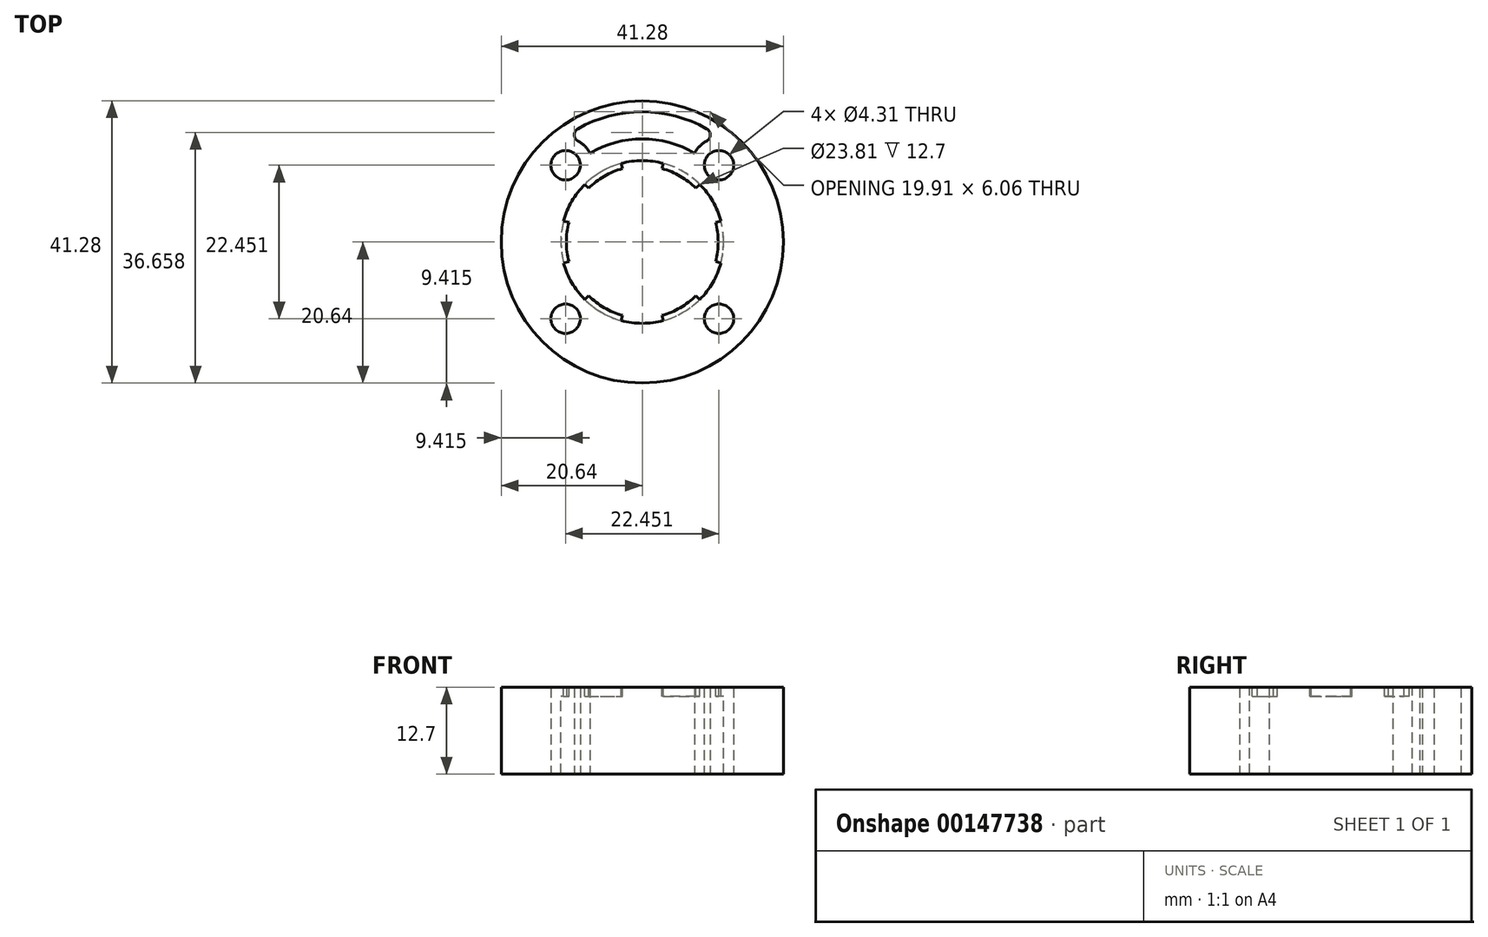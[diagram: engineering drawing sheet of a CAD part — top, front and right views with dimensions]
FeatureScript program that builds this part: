
annotation { "Feature Type Name" : "Feature", "Feature Type Description" : "" }
export const myFeature = defineFeature(function(context is Context, id is Id, definition is map)
    precondition{}
    {
        {
            var Q0;
            Q0=qCreatedBy(makeId("Top.planeOp"),FACE);
            var sketch = newSketch(context, id + "F0", { "sketchPlane" : qUnion([Q0])});
            skCircle(sketch, "E0", {"center": v(0, 0) * mm, "radius": 11.11 * mm});
            skLineSegment(sketch, "E1.bottom", {"start": v(11.23, 11.23) * mm, "end": v(-11.23, 11.23) * mm, "construction": true});
            skLineSegment(sketch, "E1.top", {"start": v(11.23, -11.23) * mm, "end": v(-11.23, -11.23) * mm, "construction": true});
            skLineSegment(sketch, "E1.left", {"start": v(11.23, 11.23) * mm, "end": v(11.23, -11.23) * mm, "construction": true});
            skLineSegment(sketch, "E1.right", {"start": v(-11.23, 11.23) * mm, "end": v(-11.23, -11.23) * mm, "construction": true});
            skCircle(sketch, "E2", {"center": v(-11.23, 11.23) * mm, "radius": 4.76 * mm, "construction": true});
            skLineSegment(sketch, "E3", {"start": v(0, 0) * mm, "end": v(0, 11.11) * mm});
            skCircle(sketch, "E4", {"center": v(-11.23, 11.23) * mm, "radius": 2.15 * mm});
            skCircle(sketch, "E5", {"center": v(-11.23, -11.23) * mm, "radius": 2.15 * mm});
            skCircle(sketch, "E6", {"center": v(11.23, -11.23) * mm, "radius": 2.15 * mm});
            skCircle(sketch, "E7", {"center": v(11.23, 11.23) * mm, "radius": 2.15 * mm});
            skCircle(sketch, "E8", {"center": v(0, 0) * mm, "radius": 20.64 * mm});
            skSolve(sketch);
        }
        {
            var Q0;
            Q0=qSketchRegion(id+"F0",true);
            extrude(context, id + "F1", {"entities" : qUnion([Q0]), "depth" : 12.7 * mm});
        }
        {
            var Q0;
            Q0=makeQuery(id+"F1.opExtrude","CAP_FACE",FACE,{"disambiguationData":[OSD([sQuery(id+"F0.wireOp",EDGE,"E0"),sQuery(id+"F0.wireOp",EDGE,"66XUYhlC-g5MV-aD6u-Z0ay-hjDTK084ohIY.top"),sQuery(id+"F0.wireOp",EDGE,"66XUYhlC-g5MV-aD6u-Z0ay-hjDTK084ohIY.left"),sQuery(id+"F0.wireOp",EDGE,"66XUYhlC-g5MV-aD6u-Z0ay-hjDTK084ohIY.right"),sQuery(id+"F0.wireOp",EDGE,"nqN0bBuQ-hJ1m-BtXy-d5jW-CiUxEReohyUV"),sQuery(id+"F0.wireOp",EDGE,"E4"),sQuery(id+"F0.wireOp",EDGE,"E5"),sQuery(id+"F0.wireOp",EDGE,"E6"),sQuery(id+"F0.wireOp",EDGE,"E7")])],"isStart":false});
            var sketch = newSketch(context, id + "F2", { "sketchPlane" : qUnion([Q0])});
            skLineSegment(sketch, "E9", {"start": v(0, 0) * mm, "end": v(0, 11.11) * mm, "construction": true});
            skLineSegment(sketch, "E10", {"start": v(0, 0) * mm, "end": v(2.88, 10.73) * mm, "construction": true});
            skLineSegment(sketch, "E11", {"start": v(0, 0) * mm, "end": v(-2.88, 10.73) * mm, "construction": true});
            skArc(sketch, "E12", {"start": v(2.88, 10.73) * mm, "mid": v(0, 11.11) * mm, "end": v(-2.88, 10.73) * mm});
            skLineSegment(sketch, "E13", {"start": v(-2.88, 10.73) * mm, "end": v(-3.08, 11.5) * mm});
            skLineSegment(sketch, "E14", {"start": v(2.88, 10.73) * mm, "end": v(3.08, 11.5) * mm});
            skArc(sketch, "E15", {"start": v(3.08, 11.5) * mm, "mid": v(0, 11.9) * mm, "end": v(-3.08, 11.5) * mm});
            skSolve(sketch);
        }
        {
            var Q0;
            Q0=qSketchRegion(id+"F2",true);
            var Q1;
            Q1=makeQuery(id+"F1.opExtrude","CAP_FACE",FACE,{"disambiguationData":[OSD([sQuery(id+"F0.wireOp",EDGE,"E0"),sQuery(id+"F0.wireOp",EDGE,"66XUYhlC-g5MV-aD6u-Z0ay-hjDTK084ohIY.top"),sQuery(id+"F0.wireOp",EDGE,"66XUYhlC-g5MV-aD6u-Z0ay-hjDTK084ohIY.left"),sQuery(id+"F0.wireOp",EDGE,"66XUYhlC-g5MV-aD6u-Z0ay-hjDTK084ohIY.right"),sQuery(id+"F0.wireOp",EDGE,"nqN0bBuQ-hJ1m-BtXy-d5jW-CiUxEReohyUV"),sQuery(id+"F0.wireOp",EDGE,"E4"),sQuery(id+"F0.wireOp",EDGE,"E5"),sQuery(id+"F0.wireOp",EDGE,"E6"),sQuery(id+"F0.wireOp",EDGE,"E7")])],"isStart":true});
            extrude(context, id + "F3", {"entities" : qUnion([Q0]), "operationType" : NewBodyOperationType.REMOVE, "endBound" : BoundingType.UP_TO_SURFACE, "oppositeDirection" : true, "endBoundEntityFace" : qUnion([Q1]), "depth" : 25.4 * mm});
        }
        {
            var Q0;
            Q0=makeQuery(id+"F3.boolean.opBoolean","COPY",FACE,{"derivedFrom":makeQuery(id+"F3.opExtrude","SWEPT_FACE",FACE,{"disambiguationData":[OSD([sQuery(id+"F2.wireOp",EDGE,"E15")])]})});
            var Q1;
            Q1=makeQuery(id+"F3.boolean.opBoolean","COPY",FACE,{"derivedFrom":makeQuery(id+"F3.opExtrude","SWEPT_FACE",FACE,{"disambiguationData":[OSD([sQuery(id+"F2.wireOp",EDGE,"E13")])]})});
            var Q2;
            Q2=makeQuery(id+"F3.boolean.opBoolean","COPY",FACE,{"derivedFrom":makeQuery(id+"F3.opExtrude","SWEPT_FACE",FACE,{"disambiguationData":[OSD([sQuery(id+"F2.wireOp",EDGE,"E14")])]})});
            var Q3;
            Q3=makeQuery(id+"F1.opExtrude","SWEPT_FACE",FACE,{"disambiguationData":[OSD([sQuery(id+"F0.wireOp",EDGE,"E0")])]});
            circularPattern(context, id + "F4", {"patternType" : PatternType.FACE, "faces" : qUnion([Q0, Q1, Q2]), "axis" : qUnion([Q3]), "angle" : 60 * degree, "instanceCount" : 6});
        }
        {
            var Q0;
            Q0=makeQuery(id+"F1.opExtrude","CAP_FACE",FACE,{"disambiguationData":[OSD([sQuery(id+"F0.wireOp",EDGE,"E0"),sQuery(id+"F0.wireOp",EDGE,"E4"),sQuery(id+"F0.wireOp",EDGE,"E5"),sQuery(id+"F0.wireOp",EDGE,"E6"),sQuery(id+"F0.wireOp",EDGE,"E7"),sQuery(id+"F0.wireOp",EDGE,"E8")])],"isStart":false});
            cPlane(context, id + "F5", {"entities" : qUnion([Q0]), "cplaneType" : CPlaneType.OFFSET, "offset" : 1.34 * mm, "oppositeDirection" : true, "width" : 152.4 * mm, "height" : 152.4 * mm});
        }
        {
            var Q0;
            Q0=makeQuery(id+"F1.opExtrude","CAP_FACE",FACE,{"disambiguationData":[OSD([sQuery(id+"F0.wireOp",EDGE,"E0"),sQuery(id+"F0.wireOp",EDGE,"E4"),sQuery(id+"F0.wireOp",EDGE,"E5"),sQuery(id+"F0.wireOp",EDGE,"E6"),sQuery(id+"F0.wireOp",EDGE,"E7"),sQuery(id+"F0.wireOp",EDGE,"E8")])],"isStart":true});
            var sketch = newSketch(context, id + "F6", { "sketchPlane" : qUnion([Q0])});
            skCircle(sketch, "E16", {"center": v(0, 0) * mm, "radius": 11.9 * mm});
            skSolve(sketch);
        }
        {
            var Q0;
            Q0=qSketchRegion(id+"F6",true);
            var Q1;
            Q1=qCreatedBy(id+"F5.planeOp",FACE);
            extrude(context, id + "F7", {"entities" : qUnion([Q0]), "operationType" : NewBodyOperationType.REMOVE, "endBound" : BoundingType.UP_TO_SURFACE, "oppositeDirection" : true, "endBoundEntityFace" : qUnion([Q1]), "depth" : 25.4 * mm});
        }
        {
            var Q0;
            Q0=makeQuery(id+"F1.opExtrude","CAP_FACE",FACE,{"disambiguationData":[OSD([sQuery(id+"F0.wireOp",EDGE,"E0"),sQuery(id+"F0.wireOp",EDGE,"E4"),sQuery(id+"F0.wireOp",EDGE,"E5"),sQuery(id+"F0.wireOp",EDGE,"E6"),sQuery(id+"F0.wireOp",EDGE,"E7"),sQuery(id+"F0.wireOp",EDGE,"E8")])],"isStart":true});
            var sketch = newSketch(context, id + "F8", { "sketchPlane" : qUnion([Q0])});
            skArc(sketch, "E17", {"start": v(7.67, -12.99) * mm, "mid": v(9.25, -14.67) * mm, "end": v(11.5, -15.18) * mm});
            skArc(sketch, "E18", {"start": v(-11.5, -15.18) * mm, "mid": v(0, -19.05) * mm, "end": v(11.5, -15.18) * mm});
            skArc(sketch, "E19", {"start": v(-7.67, -12.99) * mm, "mid": v(0, -15.08) * mm, "end": v(7.67, -12.99) * mm});
            skArc(sketch, "E20", {"start": v(-11.5, -15.18) * mm, "mid": v(-9.25, -14.67) * mm, "end": v(-7.67, -12.99) * mm});
            skSolve(sketch);
        }
        {
            var Q0;
            Q0=qSketchRegion(id+"F8",true);
            var Q1;
            Q1=makeQuery(id+"F1.opExtrude","CAP_FACE",FACE,{"disambiguationData":[OSD([sQuery(id+"F0.wireOp",EDGE,"E0"),sQuery(id+"F0.wireOp",EDGE,"E4"),sQuery(id+"F0.wireOp",EDGE,"E5"),sQuery(id+"F0.wireOp",EDGE,"E6"),sQuery(id+"F0.wireOp",EDGE,"E7"),sQuery(id+"F0.wireOp",EDGE,"E8")])],"isStart":false});
            extrude(context, id + "F9", {"entities" : qUnion([Q0]), "operationType" : NewBodyOperationType.REMOVE, "endBound" : BoundingType.UP_TO_SURFACE, "oppositeDirection" : true, "endBoundEntityFace" : qUnion([Q1]), "depth" : 25.4 * mm});
        }
        {
            var Q0;
            Q0=makeQuery(id+"FR8jf3vQ0IfpixY_1.3.F9.boolean.opBoolean","COPY",EDGE,{"derivedFrom":makeQuery(id+"FR8jf3vQ0IfpixY_1.3.F9.opExtrude","SWEPT_EDGE",EDGE,{"disambiguationData":[OSD([sQuery(id+"F8.wireOp",EDGE,"E17"),sQuery(id+"F8.wireOp",EDGE,"E18")])]})});
            var Q1;
            Q1=makeQuery(id+"F9.boolean.opBoolean","COPY",EDGE,{"derivedFrom":makeQuery(id+"F9.opExtrude","SWEPT_EDGE",EDGE,{"disambiguationData":[OSD([sQuery(id+"F8.wireOp",EDGE,"E18"),sQuery(id+"F8.wireOp",EDGE,"E20")])]})});
            var Q2;
            Q2=makeQuery(id+"F9.boolean.opBoolean","COPY",EDGE,{"derivedFrom":makeQuery(id+"F9.opExtrude","SWEPT_EDGE",EDGE,{"disambiguationData":[OSD([sQuery(id+"F8.wireOp",EDGE,"E17"),sQuery(id+"F8.wireOp",EDGE,"E18")])]})});
            var Q3;
            Q3=makeQuery(id+"FR8jf3vQ0IfpixY_1.1.F9.boolean.opBoolean","COPY",EDGE,{"derivedFrom":makeQuery(id+"FR8jf3vQ0IfpixY_1.1.F9.opExtrude","SWEPT_EDGE",EDGE,{"disambiguationData":[OSD([sQuery(id+"F8.wireOp",EDGE,"E18"),sQuery(id+"F8.wireOp",EDGE,"E20")])]})});
            var Q4;
            Q4=makeQuery(id+"FR8jf3vQ0IfpixY_1.2.F9.boolean.opBoolean","COPY",EDGE,{"derivedFrom":makeQuery(id+"FR8jf3vQ0IfpixY_1.2.F9.opExtrude","SWEPT_EDGE",EDGE,{"disambiguationData":[OSD([sQuery(id+"F8.wireOp",EDGE,"E18"),sQuery(id+"F8.wireOp",EDGE,"E20")])]})});
            var Q5;
            Q5=makeQuery(id+"FR8jf3vQ0IfpixY_1.1.F9.boolean.opBoolean","COPY",EDGE,{"derivedFrom":makeQuery(id+"FR8jf3vQ0IfpixY_1.1.F9.opExtrude","SWEPT_EDGE",EDGE,{"disambiguationData":[OSD([sQuery(id+"F8.wireOp",EDGE,"E17"),sQuery(id+"F8.wireOp",EDGE,"E18")])]})});
            var Q6;
            Q6=makeQuery(id+"FR8jf3vQ0IfpixY_1.2.F9.boolean.opBoolean","COPY",EDGE,{"derivedFrom":makeQuery(id+"FR8jf3vQ0IfpixY_1.2.F9.opExtrude","SWEPT_EDGE",EDGE,{"disambiguationData":[OSD([sQuery(id+"F8.wireOp",EDGE,"E17"),sQuery(id+"F8.wireOp",EDGE,"E18")])]})});
            var Q7;
            Q7=makeQuery(id+"FR8jf3vQ0IfpixY_1.3.F9.boolean.opBoolean","COPY",EDGE,{"derivedFrom":makeQuery(id+"FR8jf3vQ0IfpixY_1.3.F9.opExtrude","SWEPT_EDGE",EDGE,{"disambiguationData":[OSD([sQuery(id+"F8.wireOp",EDGE,"E18"),sQuery(id+"F8.wireOp",EDGE,"E20")])]})});
            fillet(context, id + "F10", {"entities" : qUnion([Q0, Q1, Q2, Q3, Q4, Q5, Q6, Q7]), "radius" : 1.02 * mm, "tangentPropagation" : true, "allowEdgeOverflow" : false});
        }
    });
